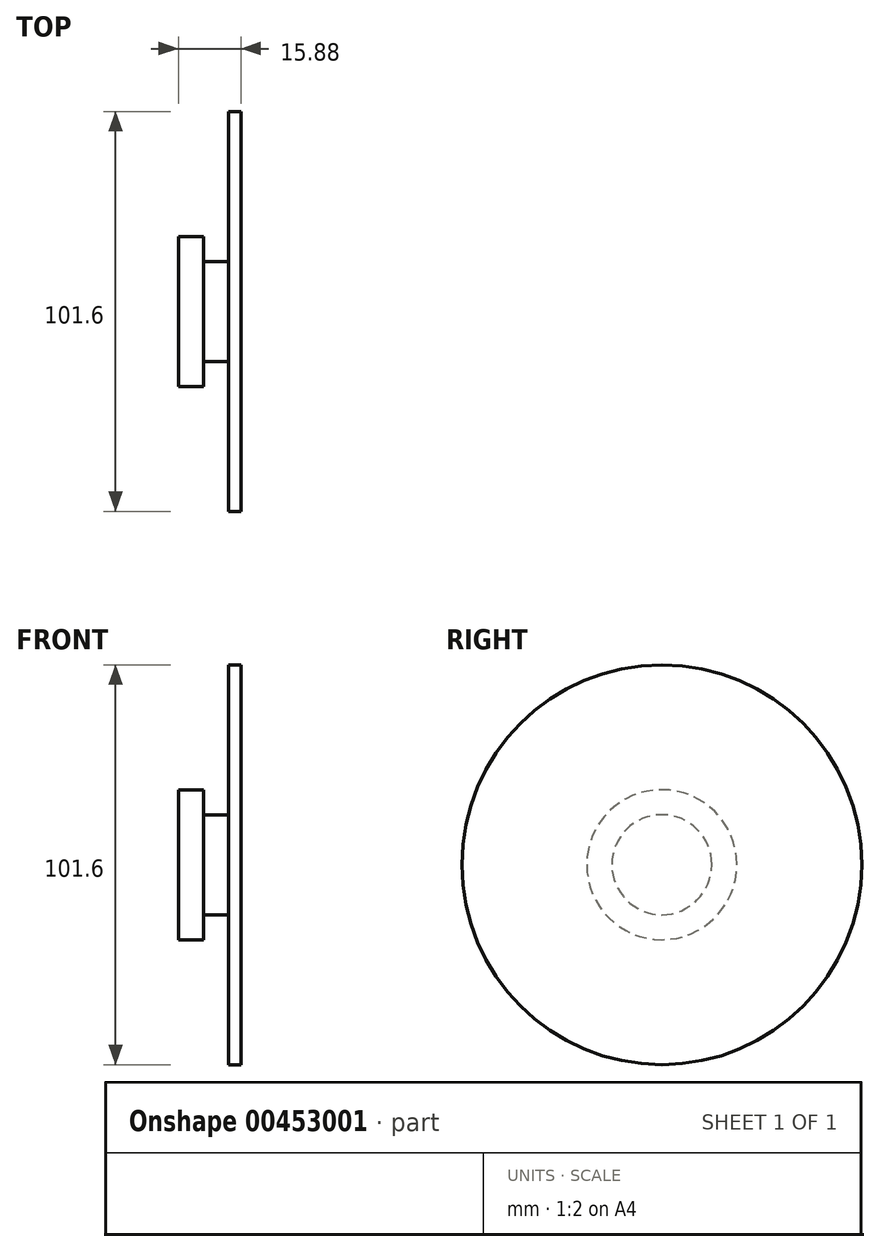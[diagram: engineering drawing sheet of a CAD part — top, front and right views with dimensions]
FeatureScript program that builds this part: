
annotation { "Feature Type Name" : "Feature", "Feature Type Description" : "" }
export const myFeature = defineFeature(function(context is Context, id is Id, definition is map)
    precondition{}
    {
        {
            var Q0;
            Q0=qCreatedBy(makeId("Front.planeOp"),FACE);
            var sketch = newSketch(context, id + "F0", { "sketchPlane" : qUnion([Q0])});
            skLineSegment(sketch, "E0.bottom", {"start": v(-37.79, -0.36) * mm, "end": v(-44.14, -0.36) * mm});
            skLineSegment(sketch, "E0.top", {"start": v(-37.79, -19.4) * mm, "end": v(-44.14, -19.4) * mm});
            skLineSegment(sketch, "E0.left", {"start": v(-37.79, -0.36) * mm, "end": v(-37.79, -19.4) * mm});
            skLineSegment(sketch, "E0.right", {"start": v(-44.14, -0.36) * mm, "end": v(-44.14, -19.4) * mm});
            skLineSegment(sketch, "E1.bottom", {"start": v(-37.79, -0.36) * mm, "end": v(-31.44, -0.36) * mm});
            skLineSegment(sketch, "E1.top", {"start": v(-37.79, -13.06) * mm, "end": v(-31.44, -13.06) * mm});
            skLineSegment(sketch, "E1.left", {"start": v(-37.79, -0.36) * mm, "end": v(-37.79, -13.06) * mm});
            skLineSegment(sketch, "E1.right", {"start": v(-31.44, -0.36) * mm, "end": v(-31.44, -13.06) * mm});
            skLineSegment(sketch, "E2.bottom", {"start": v(-31.44, -0.36) * mm, "end": v(-28.26, -0.36) * mm});
            skLineSegment(sketch, "E2.top", {"start": v(-31.44, -51.16) * mm, "end": v(-28.26, -51.16) * mm});
            skLineSegment(sketch, "E2.left", {"start": v(-31.44, -0.36) * mm, "end": v(-31.44, -51.16) * mm});
            skLineSegment(sketch, "E2.right", {"start": v(-28.26, -0.36) * mm, "end": v(-28.26, -51.16) * mm});
            skSolve(sketch);
        }
        {
            var Q0;
            Q0=makeQuery(id+"F0.imprint","IMPRINT",FACE,{"disambiguationData":[TD([[makeQuery(id+"F0.imprint","IMPRINT",EDGE,{"derivedFrom":sQuery(id+"F0.wireOp",EDGE,"E0.bottom")}),1.0]])]});
            var Q1;
            {var subQ0=sQuery(id+"F0.wireOp",EDGE,"E1.bottom");Q1=makeQuery(id+"F0.imprint","IMPRINT",FACE,{"disambiguationData":[TD([[makeQuery(id+"F0.imprint","IMPRINT",EDGE,{"derivedFrom":subQ0}),-1.0]])]});}
            var Q2;
            {var subQ3=sQuery(id+"F0.wireOp",EDGE,"E2.bottom");Q2=makeQuery(id+"F0.imprint","IMPRINT",FACE,{"disambiguationData":[TD([[makeQuery(id+"F0.imprint","IMPRINT",EDGE,{"derivedFrom":subQ3}),-1.0]])]});}
            var Q3;
            Q3=sQuery(id+"F0.wireOp",EDGE,"E0.bottom");
            revolve(context, id + "F1", {"entities" : qUnion([Q0, Q1, Q2]), "axis" : qUnion([Q3]), "revolveType" : RevolveType.FULL});
        }
    });
